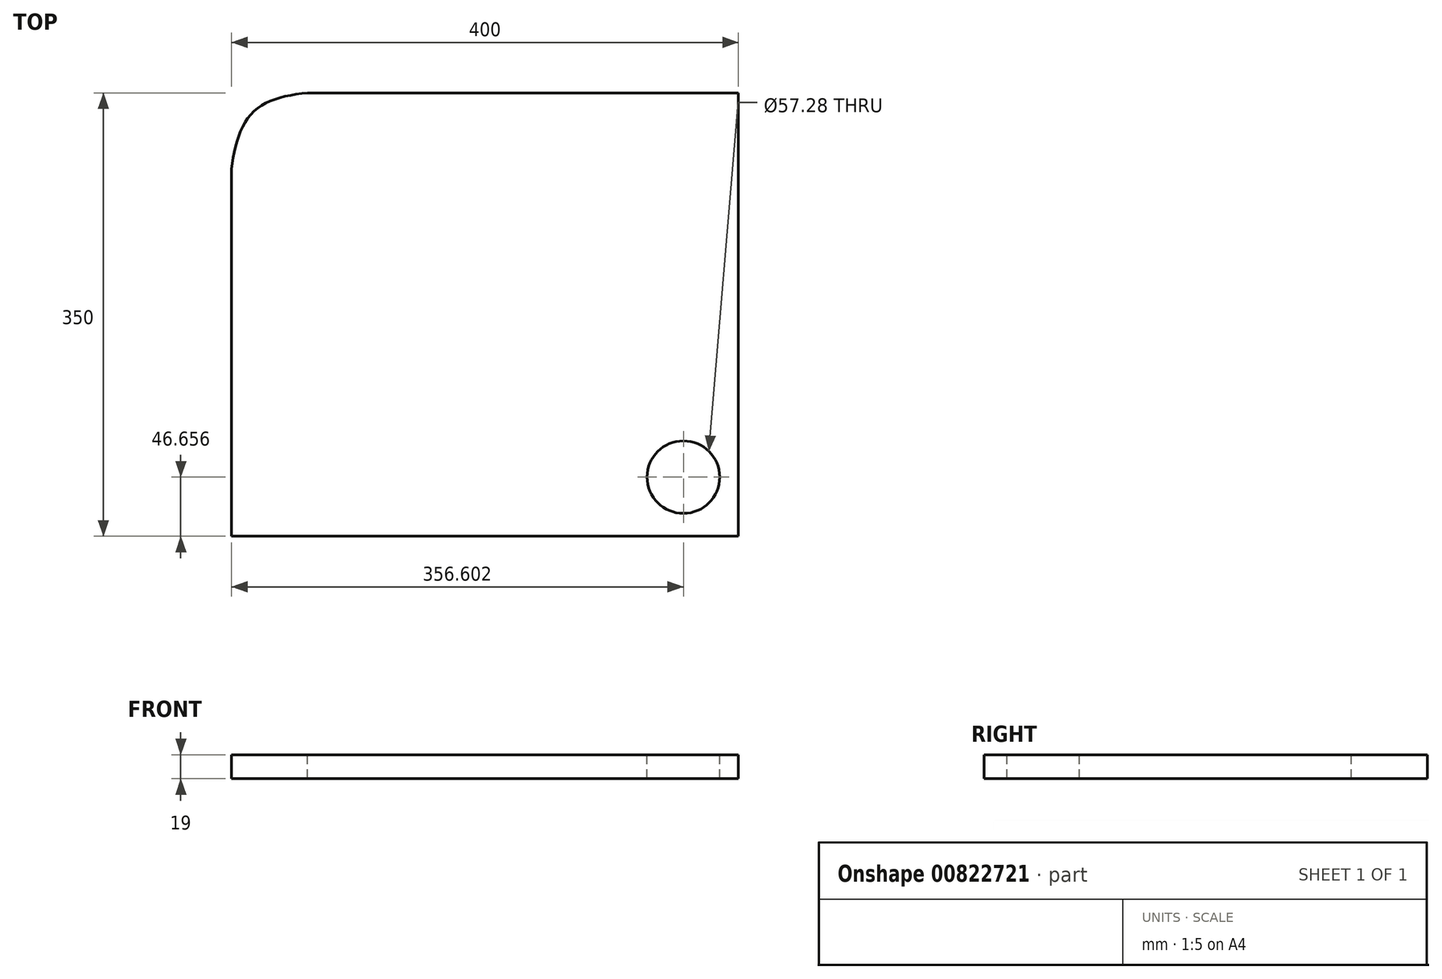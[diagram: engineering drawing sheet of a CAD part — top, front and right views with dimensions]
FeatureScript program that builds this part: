
annotation { "Feature Type Name" : "Feature", "Feature Type Description" : "" }
export const myFeature = defineFeature(function(context is Context, id is Id, definition is map)
    precondition{}
    {
        {
            var Q0;
            Q0=qCreatedBy(makeId("Top.planeOp"),FACE);
            var sketch = newSketch(context, id + "F0", { "sketchPlane" : qUnion([Q0])});
            skLineSegment(sketch, "E0.bottom", {"start": v(200, -175) * mm, "end": v(-200, -175) * mm});
            skLineSegment(sketch, "E0.top", {"start": v(200, 175) * mm, "end": v(-200, 175) * mm});
            skLineSegment(sketch, "E0.left", {"start": v(200, -175) * mm, "end": v(200, 175) * mm});
            skLineSegment(sketch, "E0.right", {"start": v(-200, -175) * mm, "end": v(-200, 175) * mm});
            skPoint(sketch, "E0.middle", {"position": v(0, 0) * mm});
            skSolve(sketch);
        }
        {
            var Q0;
            Q0 = qSketchRegion(id + "F0", true);
            extrude(context, id + "F1", {"entities" : qUnion([Q0]), "depth" : 19 * mm, "offsetDistance" : 25 * mm});
        }
        {
            var Q0;
            Q0=makeQuery(id+"F1.opExtrude","CAP_FACE",FACE,{"disambiguationData":[OSD([sQuery(id+"F0.wireOp",EDGE,"E0.bottom"),sQuery(id+"F0.wireOp",EDGE,"E0.top"),sQuery(id+"F0.wireOp",EDGE,"E0.left"),sQuery(id+"F0.wireOp",EDGE,"E0.right")])],"isStart":false});
            var sketch = newSketch(context, id + "F2", { "sketchPlane" : qUnion([Q0])});
            skFitSpline(sketch, "E1", {"points": [v(-140, 175) * mm, v(-183.46, 159.46) * mm, v(-200, 115) * mm], "startDerivative": vector(-108.4, -10.13) * mm, "endDerivative": vector(-11.9, -103.4) * mm});
            skSolve(sketch);
        }
        {
            var Q0;
            {var subQ0=sQuery(id+"F2.wireOp",EDGE,"E1");Q0=makeQuery(id+"F2.imprint","IMPRINT",FACE,{"disambiguationData":[TD([[makeQuery(id+"F2.imprint","IMPRINT",EDGE,{"derivedFrom":subQ0}),-1.0]])]});}
            extrude(context, id + "F3", {"entities" : qUnion([Q0]), "operationType" : NewBodyOperationType.REMOVE, "endBound" : BoundingType.THROUGH_ALL, "oppositeDirection" : true, "depth" : 25 * mm, "offsetDistance" : 25 * mm});
        }
        {
            var Q0;
            Q0=makeQuery(id+"F1.opExtrude","CAP_FACE",FACE,{"disambiguationData":[OSD([sQuery(id+"F0.wireOp",EDGE,"E0.bottom"),sQuery(id+"F0.wireOp",EDGE,"E0.top"),sQuery(id+"F0.wireOp",EDGE,"E0.left"),sQuery(id+"F0.wireOp",EDGE,"E0.right")])],"isStart":false});
            var sketch = newSketch(context, id + "F4", { "sketchPlane" : qUnion([Q0])});
            skCircle(sketch, "E2", {"center": v(156.6, -128.34) * mm, "radius": 28.64 * mm});
            skPoint(sketch, "E2.first.point", {"position": v(131.53, -114.5) * mm});
            skPoint(sketch, "E2.second.point", {"position": v(177.92, -147.48) * mm});
            skPoint(sketch, "E2.third.point", {"position": v(174.82, -106.25) * mm});
            skSolve(sketch);
        }
        {
            var Q0;
            Q0 = qSketchRegion(id + "F4", true);
            extrude(context, id + "F5", {"entities" : qUnion([Q0]), "operationType" : NewBodyOperationType.REMOVE, "endBound" : BoundingType.THROUGH_ALL, "oppositeDirection" : true, "depth" : 25 * mm, "offsetDistance" : 25 * mm});
        }
    });
